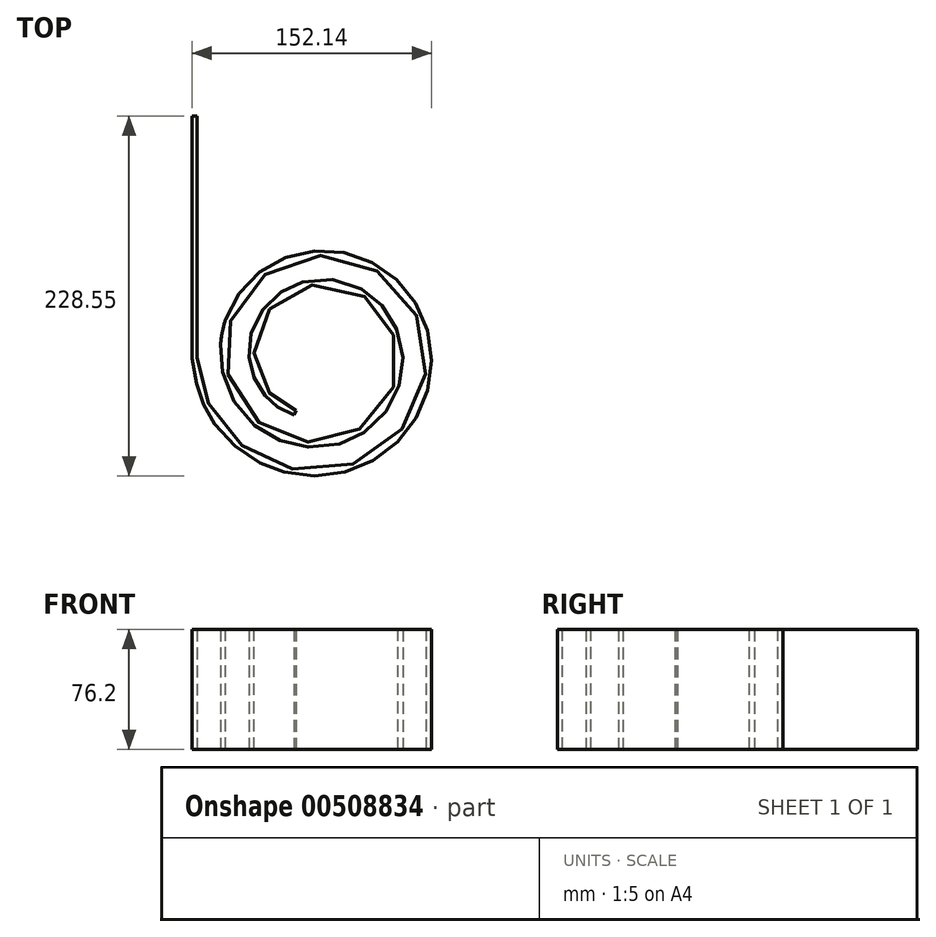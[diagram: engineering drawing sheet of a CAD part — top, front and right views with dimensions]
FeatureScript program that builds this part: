
annotation { "Feature Type Name" : "Feature", "Feature Type Description" : "" }
export const myFeature = defineFeature(function(context is Context, id is Id, definition is map)
    precondition{}
    {
        {
            var Q0;
            Q0=qCreatedBy(makeId("Top.planeOp"),FACE);
            var sketch = newSketch(context, id + "F0", { "sketchPlane" : qUnion([Q0])});
            skLineSegment(sketch, "E0", {"start": v(0, 0) * mm, "end": v(-69.85, 0) * mm, "construction": true});
            skLineSegment(sketch, "E1", {"start": v(0, 0) * mm, "end": v(0, -65.31) * mm, "construction": true});
            skLineSegment(sketch, "E2", {"start": v(0, 0) * mm, "end": v(60.77, 0) * mm, "construction": true});
            skLineSegment(sketch, "E3", {"start": v(0, 0) * mm, "end": v(0, 56.23) * mm, "construction": true});
            skLineSegment(sketch, "E4", {"start": v(0, 0) * mm, "end": v(-51.69, 0) * mm, "construction": true});
            skLineSegment(sketch, "E5", {"start": v(0, 0) * mm, "end": v(0, -47.15) * mm, "construction": true});
            skLineSegment(sketch, "E6", {"start": v(0, 0) * mm, "end": v(42.6, 0) * mm, "construction": true});
            skLineSegment(sketch, "E7", {"start": v(0, 0) * mm, "end": v(0, 38.05) * mm, "construction": true});
            skLineSegment(sketch, "E8", {"start": v(0, 0) * mm, "end": v(-33.53, 0) * mm, "construction": true});
            skLineSegment(sketch, "E9", {"start": v(0, 0) * mm, "end": v(-47.79, -47.79) * mm, "construction": true});
            skLineSegment(sketch, "E10", {"start": v(0, 0) * mm, "end": v(44.58, -44.58) * mm, "construction": true});
            skLineSegment(sketch, "E11", {"start": v(0, 0) * mm, "end": v(41.36, 41.36) * mm, "construction": true});
            skLineSegment(sketch, "E12", {"start": v(0, 0) * mm, "end": v(-38.16, 38.16) * mm, "construction": true});
            skLineSegment(sketch, "E13", {"start": v(0, 0) * mm, "end": v(-34.94, -34.94) * mm, "construction": true});
            skLineSegment(sketch, "E14", {"start": v(0, 0) * mm, "end": v(31.73, -31.73) * mm, "construction": true});
            skLineSegment(sketch, "E15", {"start": v(0, 0) * mm, "end": v(28.52, 28.52) * mm, "construction": true});
            skLineSegment(sketch, "E16", {"start": v(0, 0) * mm, "end": v(-25.31, 25.31) * mm, "construction": true});
            skLineSegment(sketch, "E17", {"start": v(0, 0) * mm, "end": v(-22.1, -22.1) * mm, "construction": true});
            skLineSegment(sketch, "E18", {"start": v(0, 0) * mm, "end": v(-63.48, -26.3) * mm, "construction": true});
            skLineSegment(sketch, "E19", {"start": v(0, 0) * mm, "end": v(-25.43, -61.39) * mm, "construction": true});
            skLineSegment(sketch, "E20", {"start": v(0, 0) * mm, "end": v(24.56, -59.3) * mm, "construction": true});
            skLineSegment(sketch, "E21", {"start": v(0, 0) * mm, "end": v(57.2, -23.69) * mm, "construction": true});
            skLineSegment(sketch, "E22", {"start": v(0, 0) * mm, "end": v(55.1, 22.82) * mm, "construction": true});
            skLineSegment(sketch, "E23", {"start": v(0, 0) * mm, "end": v(21.95, 53) * mm, "construction": true});
            skLineSegment(sketch, "E24", {"start": v(0, 0) * mm, "end": v(-21.08, 50.9) * mm, "construction": true});
            skLineSegment(sketch, "E25", {"start": v(0, 0) * mm, "end": v(-48.8, 20.22) * mm, "construction": true});
            skLineSegment(sketch, "E26", {"start": v(0, 0) * mm, "end": v(-46.7, -19.35) * mm, "construction": true});
            skLineSegment(sketch, "E27", {"start": v(0, 0) * mm, "end": v(-18.48, -44.6) * mm, "construction": true});
            skLineSegment(sketch, "E28", {"start": v(0, 0) * mm, "end": v(17.6, -42.51) * mm, "construction": true});
            skLineSegment(sketch, "E29", {"start": v(0, 0) * mm, "end": v(40.41, -16.74) * mm, "construction": true});
            skLineSegment(sketch, "E30", {"start": v(0, 0) * mm, "end": v(38.32, 15.87) * mm, "construction": true});
            skLineSegment(sketch, "E31", {"start": v(0, 0) * mm, "end": v(15, 36.22) * mm, "construction": true});
            skLineSegment(sketch, "E32", {"start": v(0, 0) * mm, "end": v(-14.13, 34.12) * mm, "construction": true});
            skLineSegment(sketch, "E33", {"start": v(0, 0) * mm, "end": v(-32.02, 13.27) * mm, "construction": true});
            skLineSegment(sketch, "E34", {"start": v(0, 0) * mm, "end": v(-29.93, -12.4) * mm, "construction": true});
            skLineSegment(sketch, "E35", {"start": v(0, 0) * mm, "end": v(-11.53, -27.83) * mm, "construction": true});
            skFitSpline(sketch, "E36", {"points": [v(-69.85, 0) * mm, v(-63.48, -26.3) * mm, v(-47.79, -47.79) * mm, v(-25.43, -61.39) * mm, v(0, -65.31) * mm, v(24.56, -59.3) * mm, v(44.58, -44.58) * mm, v(57.2, -23.69) * mm, v(60.77, 0) * mm, v(55.1, 22.82) * mm, v(41.36, 41.36) * mm, v(21.95, 53) * mm, v(0, 56.23) * mm, v(-21.08, 50.9) * mm, v(-38.16, 38.16) * mm, v(-48.8, 20.22) * mm, v(-51.69, 0) * mm, v(-46.7, -19.35) * mm, v(-34.94, -34.94) * mm, v(-18.48, -44.6) * mm, v(0, -47.15) * mm, v(17.6, -42.51) * mm, v(31.73, -31.73) * mm, v(40.41, -16.74) * mm, v(42.6, 0) * mm, v(38.32, 15.87) * mm, v(28.52, 28.52) * mm, v(15, 36.22) * mm, v(0, 38.05) * mm, v(-14.13, 34.12) * mm, v(-25.31, 25.31) * mm, v(-32.02, 13.27) * mm, v(-33.53, 0) * mm, v(-29.93, -12.4) * mm, v(-22.1, -22.1) * mm, v(-11.53, -27.83) * mm], "startDerivative": vector(125.72, -801.22) * mm, "endDerivative": vector(492.63, -215.89) * mm, "construction": true});
            skFitSpline(sketch, "E37.0", {"points": [v(-77.25, -1.16) * mm, v(-76.93, -3.25) * mm, v(-76.26, -7.48) * mm, v(-75.07, -13.97) * mm, v(-73.77, -19.44) * mm, v(-72.45, -23.82) * mm, v(-71.48, -26.54) * mm, v(-70.6, -28.72) * mm, v(-69.66, -30.88) * mm, v(-68.38, -33.52) * mm, v(-66.66, -36.59) * mm, v(-64.17, -40.54) * mm, v(-60.7, -45.22) * mm, v(-56.03, -50.4) * mm, v(-50.96, -55.1) * mm, v(-45.53, -59.32) * mm, v(-39.76, -63.02) * mm, v(-34.7, -65.66) * mm, v(-30.5, -67.48) * mm, v(-26.24, -69.1) * mm, v(-20.77, -70.75) * mm, v(-14.07, -72.1) * mm, v(-7.28, -72.84) * mm, v(-0.46, -72.93) * mm, v(6.33, -72.39) * mm, v(13.02, -71.2) * mm, v(19.56, -69.42) * mm, v(25.9, -67.02) * mm, v(31.97, -64.04) * mm, v(37.72, -60.5) * mm, v(43.1, -56.46) * mm, v(48.07, -51.93) * mm, v(52.58, -46.94) * mm, v(56.58, -41.56) * mm, v(60.04, -35.84) * mm, v(62.95, -29.83) * mm, v(65.26, -23.56) * mm, v(66.94, -17.12) * mm, v(68, -10.56) * mm, v(68.43, -3.95) * mm, v(68.21, 2.68) * mm, v(67.35, 9.24) * mm, v(65.86, 15.66) * mm, v(63.76, 21.9) * mm, v(61.06, 27.9) * mm, v(57.8, 33.6) * mm, v(54, 38.93) * mm, v(49.7, 43.86) * mm, v(44.95, 48.34) * mm, v(39.78, 52.3) * mm, v(34.26, 55.74) * mm, v(28.45, 58.6) * mm, v(22.37, 60.88) * mm, v(16.12, 62.52) * mm, v(9.75, 63.53) * mm, v(3.32, 63.9) * mm, v(-3.1, 63.62) * mm, v(-9.45, 62.7) * mm, v(-15.66, 61.14) * mm, v(-21.67, 58.97) * mm, v(-27.42, 56.2) * mm, v(-32.84, 52.86) * mm, v(-37.88, 49) * mm, v(-42.5, 44.66) * mm, v(-46.63, 39.86) * mm, v(-50.23, 34.69) * mm, v(-53.28, 29.18) * mm, v(-55.74, 23.4) * mm, v(-57.58, 17.39) * mm, v(-58.78, 11.25) * mm, v(-59.24, 6.07) * mm, v(-59.28, 1.92) * mm, v(-59.1, -2.23) * mm, v(-58.47, -7.38) * mm, v(-57.07, -13.42) * mm, v(-55.05, -19.27) * mm, v(-52.42, -24.87) * mm, v(-49.22, -30.13) * mm, v(-45.49, -35.01) * mm, v(-41.27, -39.46) * mm, v(-36.59, -43.43) * mm, v(-31.53, -46.85) * mm, v(-27.05, -49.22) * mm, v(-23.33, -50.83) * mm, v(-19.52, -52.22) * mm, v(-14.65, -53.57) * mm, v(-8.68, -54.53) * mm, v(-2.66, -54.84) * mm, v(3.37, -54.48) * mm, v(9.28, -53.47) * mm, v(15.04, -51.8) * mm, v(19.64, -49.91) * mm, v(23.18, -48.09) * mm, v(26.6, -46.08) * mm, v(30.65, -43.22) * mm, v(35.08, -39.28) * mm, v(39.03, -34.86) * mm, v(42.45, -30.05) * mm, v(45.29, -24.9) * mm, v(47.15, -20.37) * mm, v(48.32, -16.64) * mm, v(49.27, -12.86) * mm, v(50.04, -8.06) * mm, v(50.3, -2.24) * mm, v(49.9, 3.57) * mm, v(48.81, 9.26) * mm, v(47.38, 13.85) * mm, v(45.91, 17.4) * mm, v(44.24, 20.86) * mm, v(41.78, 24.96) * mm, v(38.28, 29.5) * mm, v(34.95, 32.9) * mm, v(32.06, 35.37) * mm, v(29.03, 37.65) * mm, v(25.01, 40.15) * mm, v(19.88, 42.54) * mm, v(14.5, 44.3) * mm, v(8.97, 45.36) * mm, v(3.38, 45.76) * mm, v(-2.21, 45.48) * mm, v(-7.7, 44.52) * mm, v(-12.13, 43.18) * mm, v(-15.55, 41.78) * mm, v(-18.88, 40.16) * mm, v(-22.82, 37.77) * mm, v(-27.13, 34.34) * mm, v(-30.33, 31.06) * mm, v(-32.62, 28.22) * mm, v(-34.72, 25.24) * mm, v(-36.97, 21.3) * mm, v(-38.7, 17.11) * mm, v(-39.75, 13.65) * mm, v(-40.57, 10.13) * mm, v(-41.17, 5.68) * mm, v(-41.18, 1.19) * mm, v(-40.83, -2.38) * mm, v(-40.26, -5.9) * mm, v(-39.1, -10.18) * mm, v(-37.43, -14.26) * mm, v(-35.78, -17.38) * mm, v(-34.39, -19.64) * mm, v(-32.84, -21.82) * mm, v(-31.13, -23.9) * mm, v(-29.57, -25.52) * mm, v(-28.24, -26.74) * mm, v(-27.2, -27.63) * mm, v(-26.13, -28.47) * mm, v(-25.04, -29.25) * mm, v(-23.94, -29.97) * mm, v(-22.49, -30.86) * mm, v(-20.68, -31.85) * mm, v(-17.84, -33.24) * mm, v(-15.82, -34.13) * mm, v(-14.53, -34.7) * mm]});
            skFitSpline(sketch, "E38.0", {"points": [v(-80.39, -1.65) * mm, v(-80.06, -3.74) * mm, v(-79.4, -8) * mm, v(-78.18, -14.61) * mm, v(-76.84, -20.25) * mm, v(-75.46, -24.8) * mm, v(-74.45, -27.66) * mm, v(-73.54, -29.94) * mm, v(-72.54, -32.22) * mm, v(-71.2, -34.99) * mm, v(-69.4, -38.2) * mm, v(-66.78, -42.35) * mm, v(-63.15, -47.24) * mm, v(-58.3, -52.63) * mm, v(-53.02, -57.52) * mm, v(-47.37, -61.91) * mm, v(-41.35, -65.77) * mm, v(-36.07, -68.52) * mm, v(-31.7, -70.42) * mm, v(-27.25, -72.12) * mm, v(-21.55, -73.84) * mm, v(-14.56, -75.25) * mm, v(-7.48, -76.01) * mm, v(-0.35, -76.11) * mm, v(6.74, -75.54) * mm, v(13.72, -74.31) * mm, v(20.54, -72.44) * mm, v(27.16, -69.94) * mm, v(33.5, -66.82) * mm, v(39.5, -63.13) * mm, v(45.13, -58.9) * mm, v(50.32, -54.17) * mm, v(55.04, -48.96) * mm, v(59.22, -43.34) * mm, v(62.84, -37.36) * mm, v(65.87, -31.07) * mm, v(68.3, -24.51) * mm, v(70.05, -17.78) * mm, v(71.16, -10.92) * mm, v(71.6, -4) * mm, v(71.38, 2.94) * mm, v(70.48, 9.8) * mm, v(68.92, 16.53) * mm, v(66.73, 23.06) * mm, v(63.9, 29.35) * mm, v(60.47, 35.31) * mm, v(56.5, 40.9) * mm, v(52, 46.06) * mm, v(47, 50.76) * mm, v(41.59, 54.92) * mm, v(35.8, 58.52) * mm, v(29.7, 61.52) * mm, v(23.33, 63.9) * mm, v(16.77, 65.63) * mm, v(10.1, 66.7) * mm, v(3.35, 67.08) * mm, v(-3.4, 66.8) * mm, v(-10.07, 65.81) * mm, v(-16.59, 64.18) * mm, v(-22.9, 61.9) * mm, v(-28.95, 58.99) * mm, v(-34.64, 55.48) * mm, v(-39.93, 51.43) * mm, v(-44.79, 46.86) * mm, v(-49.14, 41.81) * mm, v(-52.93, 36.37) * mm, v(-56.14, 30.58) * mm, v(-58.73, 24.48) * mm, v(-60.66, 18.16) * mm, v(-61.93, 11.7) * mm, v(-62.41, 6.24) * mm, v(-62.46, 1.87) * mm, v(-62.27, -2.5) * mm, v(-61.6, -7.93) * mm, v(-60.13, -14.3) * mm, v(-58, -20.46) * mm, v(-55.23, -26.37) * mm, v(-51.85, -31.93) * mm, v(-47.91, -37.08) * mm, v(-43.45, -41.77) * mm, v(-38.5, -45.96) * mm, v(-33.17, -49.57) * mm, v(-28.44, -52.08) * mm, v(-24.5, -53.78) * mm, v(-20.48, -55.25) * mm, v(-15.33, -56.67) * mm, v(-9.02, -57.7) * mm, v(-2.65, -58.02) * mm, v(3.73, -57.64) * mm, v(10, -56.57) * mm, v(16.08, -54.81) * mm, v(20.97, -52.8) * mm, v(24.72, -50.87) * mm, v(28.34, -48.74) * mm, v(32.62, -45.7) * mm, v(37.32, -41.53) * mm, v(41.52, -36.84) * mm, v(45.14, -31.74) * mm, v(48.15, -26.27) * mm, v(50.13, -21.46) * mm, v(51.38, -17.5) * mm, v(52.38, -13.48) * mm, v(53.2, -8.38) * mm, v(53.49, -2.2) * mm, v(53.05, 3.98) * mm, v(51.9, 10.03) * mm, v(50.37, 14.91) * mm, v(48.81, 18.7) * mm, v(47.03, 22.38) * mm, v(44.4, 26.76) * mm, v(40.69, 31.58) * mm, v(37.14, 35.21) * mm, v(34.05, 37.84) * mm, v(30.82, 40.28) * mm, v(26.53, 42.94) * mm, v(21.05, 45.5) * mm, v(15.29, 47.38) * mm, v(9.38, 48.52) * mm, v(3.41, 48.94) * mm, v(-2.56, 48.64) * mm, v(-8.44, 47.62) * mm, v(-13.18, 46.18) * mm, v(-16.84, 44.68) * mm, v(-19.52, 43.38) * mm, v(-22.1, 41.92) * mm, v(-25.41, 39.77) * mm, v(-29.26, 36.7) * mm, v(-32.7, 33.19) * mm, v(-35.16, 30.13) * mm, v(-37.4, 26.94) * mm, v(-39.83, 22.7) * mm, v(-41.69, 18.2) * mm, v(-42.82, 14.47) * mm, v(-43.7, 10.69) * mm, v(-44.21, 6.85) * mm, v(-44.35, 3) * mm, v(-44.26, 0.1) * mm, v(-43.99, -2.79) * mm, v(-43.52, -5.63) * mm, v(-42.87, -8.43) * mm, v(-42.04, -11.16) * mm, v(-41.04, -13.84) * mm, v(-39.87, -16.43) * mm, v(-38.54, -18.95) * mm, v(-37.04, -21.4) * mm, v(-35.36, -23.75) * mm, v(-33.5, -26) * mm, v(-31.8, -27.77) * mm, v(-30.35, -29.12) * mm, v(-29.21, -30.09) * mm, v(-28.02, -31.02) * mm, v(-26.83, -31.87) * mm, v(-25.64, -32.65) * mm, v(-24.07, -33.6) * mm, v(-22.14, -34.67) * mm, v(-19.16, -36.13) * mm, v(-17.1, -37.04) * mm, v(-15.8, -37.6) * mm]});
            skLineSegment(sketch, "E39", {"start": v(-77.34, 0) * mm, "end": v(-77.34, 152.4) * mm});
            skLineSegment(sketch, "E40.0", {"start": v(-80.52, 0) * mm, "end": v(-80.52, 152.4) * mm});
            skLineSegment(sketch, "E41", {"start": v(-62.36, 0) * mm, "end": v(-62.36, 152.4) * mm});
            skFitSpline(sketch, "E42.trimOffspring", {"points": [v(-80.39, -1.65) * mm, v(-80.06, -3.74) * mm, v(-79.4, -8) * mm, v(-78.18, -14.61) * mm, v(-76.84, -20.25) * mm, v(-75.46, -24.8) * mm, v(-74.45, -27.66) * mm, v(-73.54, -29.94) * mm, v(-72.54, -32.22) * mm, v(-71.2, -34.99) * mm, v(-69.4, -38.2) * mm, v(-66.78, -42.35) * mm, v(-63.15, -47.24) * mm, v(-58.3, -52.63) * mm, v(-53.02, -57.52) * mm, v(-47.37, -61.91) * mm, v(-41.35, -65.77) * mm, v(-36.07, -68.52) * mm, v(-31.7, -70.42) * mm, v(-27.25, -72.12) * mm, v(-21.55, -73.84) * mm, v(-14.56, -75.25) * mm, v(-7.48, -76.01) * mm, v(-0.35, -76.11) * mm, v(6.74, -75.54) * mm, v(13.72, -74.31) * mm, v(20.54, -72.44) * mm, v(27.16, -69.94) * mm, v(33.5, -66.82) * mm, v(39.5, -63.13) * mm, v(45.13, -58.9) * mm, v(50.32, -54.17) * mm, v(55.04, -48.96) * mm, v(59.22, -43.34) * mm, v(62.84, -37.36) * mm, v(65.87, -31.07) * mm, v(68.3, -24.51) * mm, v(70.05, -17.78) * mm, v(71.16, -10.92) * mm, v(71.6, -4) * mm, v(71.38, 2.94) * mm, v(70.48, 9.8) * mm, v(68.92, 16.53) * mm, v(66.73, 23.06) * mm, v(63.9, 29.35) * mm, v(60.47, 35.31) * mm, v(56.5, 40.9) * mm, v(52, 46.06) * mm, v(47, 50.76) * mm, v(41.59, 54.92) * mm, v(35.8, 58.52) * mm, v(29.7, 61.52) * mm, v(23.33, 63.9) * mm, v(16.77, 65.63) * mm, v(10.1, 66.7) * mm, v(3.35, 67.08) * mm, v(-3.4, 66.8) * mm, v(-10.07, 65.81) * mm, v(-16.59, 64.18) * mm, v(-22.9, 61.9) * mm, v(-28.95, 58.99) * mm, v(-34.64, 55.48) * mm, v(-39.93, 51.43) * mm, v(-44.79, 46.86) * mm, v(-49.14, 41.81) * mm, v(-52.93, 36.37) * mm, v(-56.14, 30.58) * mm, v(-58.73, 24.48) * mm, v(-60.66, 18.16) * mm, v(-61.93, 11.7) * mm, v(-62.41, 6.24) * mm, v(-62.46, 1.87) * mm, v(-62.27, -2.5) * mm, v(-61.6, -7.93) * mm, v(-60.13, -14.3) * mm, v(-58, -20.46) * mm, v(-55.23, -26.37) * mm, v(-51.85, -31.93) * mm, v(-47.91, -37.08) * mm, v(-43.45, -41.77) * mm, v(-38.5, -45.96) * mm, v(-33.17, -49.57) * mm, v(-28.44, -52.08) * mm, v(-24.5, -53.78) * mm, v(-20.48, -55.25) * mm, v(-15.33, -56.67) * mm, v(-9.02, -57.7) * mm, v(-2.65, -58.02) * mm, v(3.73, -57.64) * mm, v(10, -56.57) * mm, v(16.08, -54.81) * mm, v(20.97, -52.8) * mm, v(24.72, -50.87) * mm, v(28.34, -48.74) * mm, v(32.62, -45.7) * mm, v(37.32, -41.53) * mm, v(41.52, -36.84) * mm, v(45.14, -31.74) * mm, v(48.15, -26.27) * mm, v(50.13, -21.46) * mm, v(51.38, -17.5) * mm, v(52.38, -13.48) * mm, v(53.2, -8.38) * mm, v(53.49, -2.2) * mm, v(53.05, 3.98) * mm, v(51.9, 10.03) * mm, v(50.37, 14.91) * mm, v(48.81, 18.7) * mm, v(47.03, 22.38) * mm, v(44.4, 26.76) * mm, v(40.69, 31.58) * mm, v(37.14, 35.21) * mm, v(34.05, 37.84) * mm, v(30.82, 40.28) * mm, v(26.53, 42.94) * mm, v(21.05, 45.5) * mm, v(15.29, 47.38) * mm, v(9.38, 48.52) * mm, v(3.41, 48.94) * mm, v(-2.56, 48.64) * mm, v(-8.44, 47.62) * mm, v(-13.18, 46.18) * mm, v(-16.84, 44.68) * mm, v(-19.52, 43.38) * mm, v(-22.1, 41.92) * mm, v(-25.41, 39.77) * mm, v(-29.26, 36.7) * mm, v(-32.7, 33.19) * mm, v(-35.16, 30.13) * mm, v(-37.4, 26.94) * mm, v(-39.83, 22.7) * mm, v(-41.69, 18.2) * mm, v(-42.82, 14.47) * mm, v(-43.7, 10.69) * mm, v(-44.21, 6.85) * mm, v(-44.35, 3) * mm, v(-44.26, 0.1) * mm, v(-43.99, -2.79) * mm, v(-43.52, -5.63) * mm, v(-42.87, -8.43) * mm, v(-42.04, -11.16) * mm, v(-41.04, -13.84) * mm, v(-39.87, -16.43) * mm, v(-38.54, -18.95) * mm, v(-37.04, -21.4) * mm, v(-35.36, -23.75) * mm, v(-33.5, -26) * mm, v(-31.8, -27.77) * mm, v(-30.35, -29.12) * mm, v(-29.21, -30.09) * mm, v(-28.02, -31.02) * mm, v(-26.83, -31.87) * mm, v(-25.64, -32.65) * mm, v(-24.07, -33.6) * mm, v(-22.14, -34.67) * mm, v(-19.16, -36.13) * mm, v(-17.1, -37.04) * mm, v(-15.8, -37.6) * mm]});
            skFitSpline(sketch, "E43.trimOffspring", {"points": [v(-77.25, -1.16) * mm, v(-76.93, -3.25) * mm, v(-76.26, -7.48) * mm, v(-75.07, -13.97) * mm, v(-73.77, -19.44) * mm, v(-72.45, -23.82) * mm, v(-71.48, -26.54) * mm, v(-70.6, -28.72) * mm, v(-69.66, -30.88) * mm, v(-68.38, -33.52) * mm, v(-66.66, -36.59) * mm, v(-64.17, -40.54) * mm, v(-60.7, -45.22) * mm, v(-56.03, -50.4) * mm, v(-50.96, -55.1) * mm, v(-45.53, -59.32) * mm, v(-39.76, -63.02) * mm, v(-34.7, -65.66) * mm, v(-30.5, -67.48) * mm, v(-26.24, -69.1) * mm, v(-20.77, -70.75) * mm, v(-14.07, -72.1) * mm, v(-7.28, -72.84) * mm, v(-0.46, -72.93) * mm, v(6.33, -72.39) * mm, v(13.02, -71.2) * mm, v(19.56, -69.42) * mm, v(25.9, -67.02) * mm, v(31.97, -64.04) * mm, v(37.72, -60.5) * mm, v(43.1, -56.46) * mm, v(48.07, -51.93) * mm, v(52.58, -46.94) * mm, v(56.58, -41.56) * mm, v(60.04, -35.84) * mm, v(62.95, -29.83) * mm, v(65.26, -23.56) * mm, v(66.94, -17.12) * mm, v(68, -10.56) * mm, v(68.43, -3.95) * mm, v(68.21, 2.68) * mm, v(67.35, 9.24) * mm, v(65.86, 15.66) * mm, v(63.76, 21.9) * mm, v(61.06, 27.9) * mm, v(57.8, 33.6) * mm, v(54, 38.93) * mm, v(49.7, 43.86) * mm, v(44.95, 48.34) * mm, v(39.78, 52.3) * mm, v(34.26, 55.74) * mm, v(28.45, 58.6) * mm, v(22.37, 60.88) * mm, v(16.12, 62.52) * mm, v(9.75, 63.53) * mm, v(3.32, 63.9) * mm, v(-3.1, 63.62) * mm, v(-9.45, 62.7) * mm, v(-15.66, 61.14) * mm, v(-21.67, 58.97) * mm, v(-27.42, 56.2) * mm, v(-32.84, 52.86) * mm, v(-37.88, 49) * mm, v(-42.5, 44.66) * mm, v(-46.63, 39.86) * mm, v(-50.23, 34.69) * mm, v(-53.28, 29.18) * mm, v(-55.74, 23.4) * mm, v(-57.58, 17.39) * mm, v(-58.78, 11.25) * mm, v(-59.24, 6.07) * mm, v(-59.28, 1.92) * mm, v(-59.1, -2.23) * mm, v(-58.47, -7.38) * mm, v(-57.07, -13.42) * mm, v(-55.05, -19.27) * mm, v(-52.42, -24.87) * mm, v(-49.22, -30.13) * mm, v(-45.49, -35.01) * mm, v(-41.27, -39.46) * mm, v(-36.59, -43.43) * mm, v(-31.53, -46.85) * mm, v(-27.05, -49.22) * mm, v(-23.33, -50.83) * mm, v(-19.52, -52.22) * mm, v(-14.65, -53.57) * mm, v(-8.68, -54.53) * mm, v(-2.66, -54.84) * mm, v(3.37, -54.48) * mm, v(9.28, -53.47) * mm, v(15.04, -51.8) * mm, v(19.64, -49.91) * mm, v(23.18, -48.09) * mm, v(26.6, -46.08) * mm, v(30.65, -43.22) * mm, v(35.08, -39.28) * mm, v(39.03, -34.86) * mm, v(42.45, -30.05) * mm, v(45.29, -24.9) * mm, v(47.15, -20.37) * mm, v(48.32, -16.64) * mm, v(49.27, -12.86) * mm, v(50.04, -8.06) * mm, v(50.3, -2.24) * mm, v(49.9, 3.57) * mm, v(48.81, 9.26) * mm, v(47.38, 13.85) * mm, v(45.91, 17.4) * mm, v(44.24, 20.86) * mm, v(41.78, 24.96) * mm, v(38.28, 29.5) * mm, v(34.95, 32.9) * mm, v(32.06, 35.37) * mm, v(29.03, 37.65) * mm, v(25.01, 40.15) * mm, v(19.88, 42.54) * mm, v(14.5, 44.3) * mm, v(8.97, 45.36) * mm, v(3.38, 45.76) * mm, v(-2.21, 45.48) * mm, v(-7.7, 44.52) * mm, v(-12.13, 43.18) * mm, v(-15.55, 41.78) * mm, v(-18.88, 40.16) * mm, v(-22.82, 37.77) * mm, v(-27.13, 34.34) * mm, v(-30.33, 31.06) * mm, v(-32.62, 28.22) * mm, v(-34.72, 25.24) * mm, v(-36.97, 21.3) * mm, v(-38.7, 17.11) * mm, v(-39.75, 13.65) * mm, v(-40.57, 10.13) * mm, v(-41.17, 5.68) * mm, v(-41.18, 1.19) * mm, v(-40.83, -2.38) * mm, v(-40.26, -5.9) * mm, v(-39.1, -10.18) * mm, v(-37.43, -14.26) * mm, v(-35.78, -17.38) * mm, v(-34.39, -19.64) * mm, v(-32.84, -21.82) * mm, v(-31.13, -23.9) * mm, v(-29.57, -25.52) * mm, v(-28.24, -26.74) * mm, v(-27.2, -27.63) * mm, v(-26.13, -28.47) * mm, v(-25.04, -29.25) * mm, v(-23.94, -29.97) * mm, v(-22.49, -30.86) * mm, v(-20.68, -31.85) * mm, v(-17.84, -33.24) * mm, v(-15.82, -34.13) * mm, v(-14.53, -34.7) * mm]});
            skLineSegment(sketch, "E44", {"start": v(-77.25, -1.16) * mm, "end": v(-77.34, 0) * mm});
            skLineSegment(sketch, "E45", {"start": v(-62.36, 152.4) * mm, "end": v(-59.18, 152.4) * mm});
            skLineSegment(sketch, "E46", {"start": v(-77.34, 152.4) * mm, "end": v(-80.52, 152.4) * mm});
            skLineSegment(sketch, "E47", {"start": v(-80.39, -1.65) * mm, "end": v(-80.52, 0) * mm});
            skLineSegment(sketch, "E48", {"start": v(-14.53, -34.7) * mm, "end": v(-15.8, -37.6) * mm});
            skLineSegment(sketch, "E49.trimOffspring", {"start": v(-59.18, 22.84) * mm, "end": v(-59.18, 152.4) * mm});
            skLineSegment(sketch, "E50", {"start": v(-59.2, 0) * mm, "end": v(-59.18, 0) * mm});
            skLineSegment(sketch, "E51", {"start": v(-59.18, 5.94) * mm, "end": v(-59.18, 0) * mm});
            skLineSegment(sketch, "E52", {"start": v(-62.36, 0) * mm, "end": v(-62.37, 0) * mm});
            skSolve(sketch);
        }
        {
            var Q0;
            Q0=makeQuery(id+"F0.imprint","IMPRINT",FACE,{"disambiguationData":[TD([[makeQuery(id+"F0.imprint","IMPRINT",EDGE,{"derivedFrom":sQuery(id+"F0.wireOp",EDGE,"E37.0")}),-1.0]])]});
            extrude(context, id + "F1", {"entities" : qUnion([Q0]), "depth" : 76.2 * mm});
        }
    });
